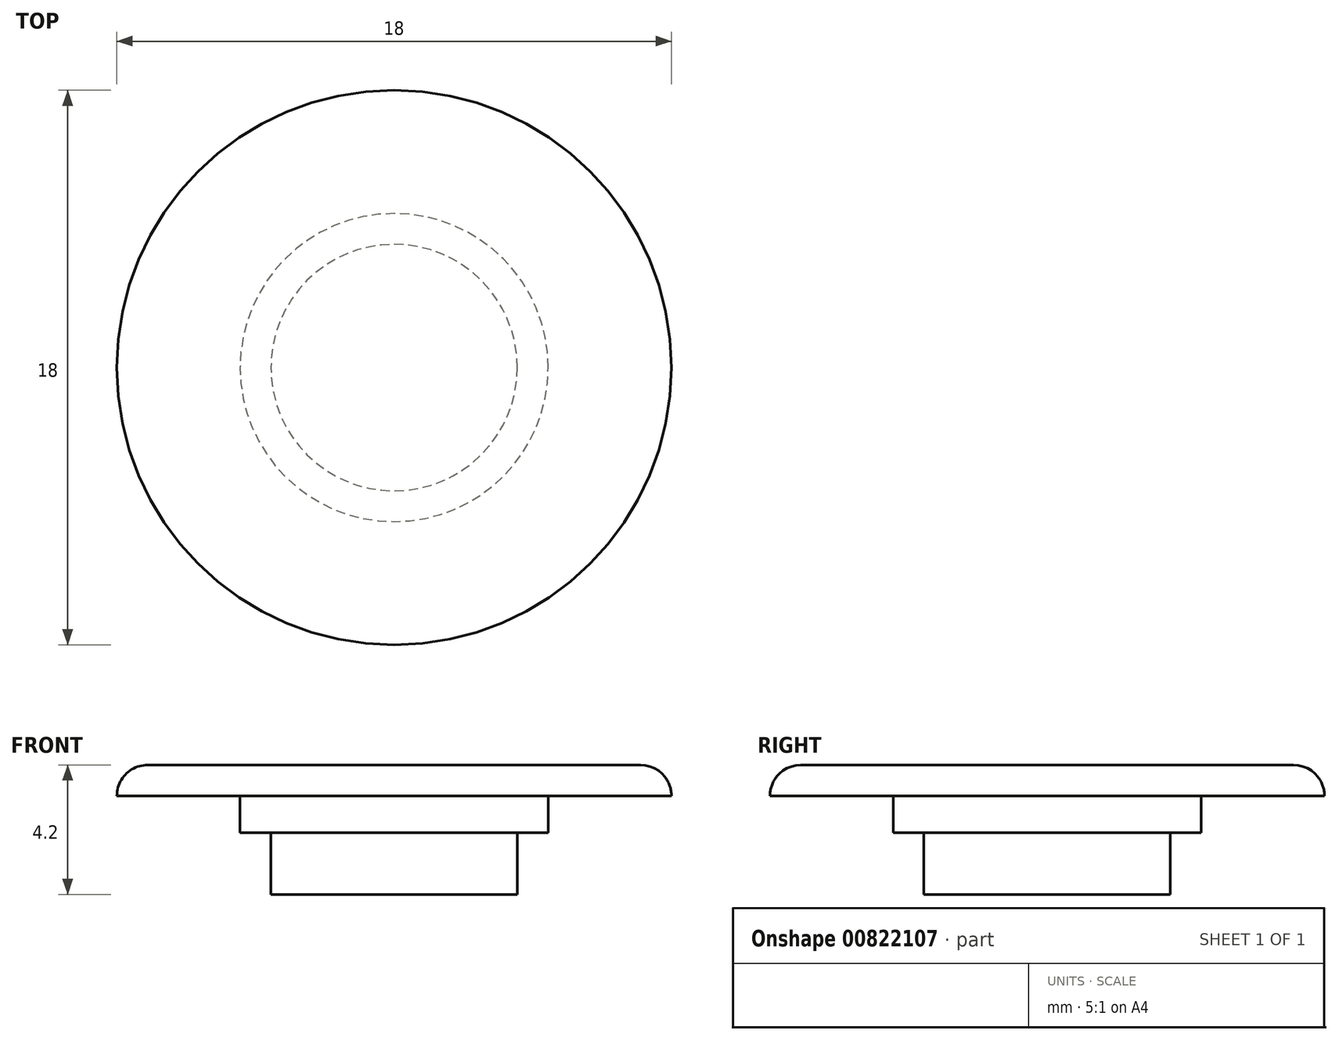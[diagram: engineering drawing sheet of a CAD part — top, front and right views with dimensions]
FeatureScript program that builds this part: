
annotation { "Feature Type Name" : "Feature", "Feature Type Description" : "" }
export const myFeature = defineFeature(function(context is Context, id is Id, definition is map)
    precondition{}
    {
        {
            var Q0;
            Q0=qCreatedBy(makeId("Front.planeOp"),FACE);
            var sketch = newSketch(context, id + "F0", { "sketchPlane" : qUnion([Q0])});
            skLineSegment(sketch, "E0", {"start": v(0, 0) * mm, "end": v(4, 0) * mm});
            skLineSegment(sketch, "E1", {"start": v(4, 0) * mm, "end": v(4, 2) * mm});
            skLineSegment(sketch, "E2", {"start": v(4, 2) * mm, "end": v(5, 2) * mm});
            skLineSegment(sketch, "E3", {"start": v(5, 2) * mm, "end": v(5, 3.2) * mm});
            skLineSegment(sketch, "E4", {"start": v(5, 3.2) * mm, "end": v(9, 3.2) * mm});
            skLineSegment(sketch, "E5", {"start": v(9, 3.2) * mm, "end": v(9, 4.2) * mm});
            skLineSegment(sketch, "E6", {"start": v(9, 4.2) * mm, "end": v(0, 4.2) * mm});
            skLineSegment(sketch, "E7", {"start": v(0, 4.2) * mm, "end": v(0, 0) * mm});
            skSolve(sketch);
        }
        {
            var Q0;
            Q0=makeQuery(id+"F0.imprint","IMPRINT",FACE,{"disambiguationData":[TD([[makeQuery(id+"F0.imprint","IMPRINT",EDGE,{"derivedFrom":sQuery(id+"F0.wireOp",EDGE,"E0")}),1.0]])]});
            var Q1;
            Q1=sQuery(id+"F0.wireOp",EDGE,"E7");
            revolve(context, id + "F1", {"surfaceOperationType" : NewSurfaceOperationType.NEW, "entities" : qUnion([Q0]), "axis" : qUnion([Q1]), "revolveType" : RevolveType.FULL});
        }
        {
            var Q0;
            Q0=makeQuery(id+"F1.opRevolve","SWEPT_EDGE",EDGE,{"disambiguationData":[OSD([sQuery(id+"F0.wireOp",EDGE,"E5"),sQuery(id+"F0.wireOp",EDGE,"E6")])]});
            fillet(context, id + "F2", {"entities" : qUnion([Q0]), "radius" : 1 * mm, "tangentPropagation" : true, "allowEdgeOverflow" : false});
        }
    });
